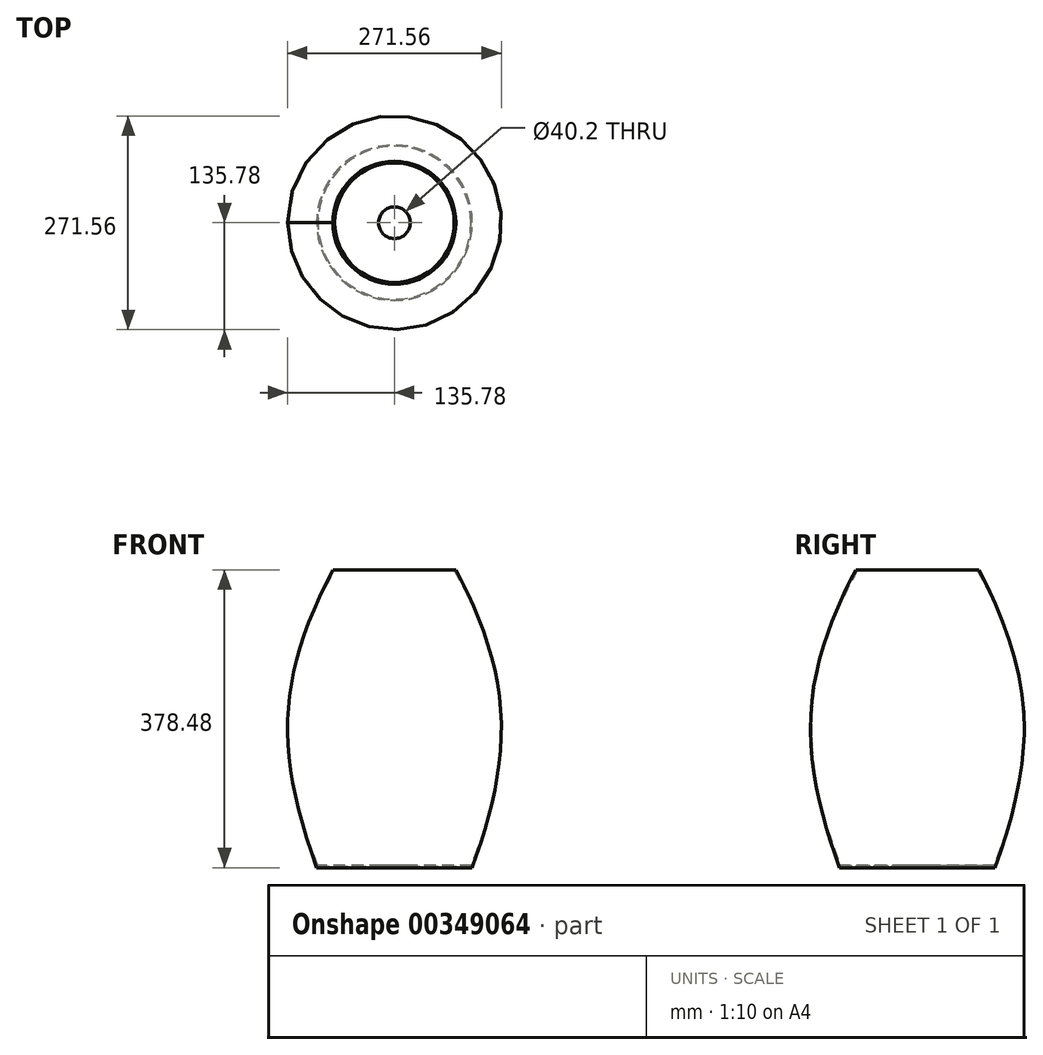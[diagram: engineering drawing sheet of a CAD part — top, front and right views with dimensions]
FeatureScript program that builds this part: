
annotation { "Feature Type Name" : "Feature", "Feature Type Description" : "" }
export const myFeature = defineFeature(function(context is Context, id is Id, definition is map)
    precondition{}
    {
        {
            var Q0;
            Q0=qCreatedBy(makeId("Top.planeOp"),FACE);
            var sketch = newSketch(context, id + "F0", { "sketchPlane" : qUnion([Q0])});
            skCircle(sketch, "E0", {"center": v(0, 0) * mm, "radius": 98.5 * mm});
            skLineSegment(sketch, "E1", {"start": v(0, 0) * mm, "end": v(133.35, 0) * mm, "construction": true});
            skLineSegment(sketch, "E2", {"start": v(133.35, 0) * mm, "end": v(0, 0) * mm, "construction": true});
            skLineSegment(sketch, "E3", {"start": v(0, 0) * mm, "end": v(0, 114.26) * mm, "construction": true});
            skSolve(sketch);
        }
        {
            var Q0;
            Q0 = qSketchRegion(id + "F0", true);
            extrude(context, id + "F1", {"entities" : qUnion([Q0]), "depth" : 3 * mm});
        }
        {
            var Q0;
            Q0=sQuery(id+"F0.wireOp",VERTEX,"E1.start");
            var Q1;
            Q1=makeQuery(id+"F1.opExtrude","SWEPT_BODY",BODY,{"disambiguationData":[OSD([sQuery(id+"F0.wireOp",EDGE,"E0")])]});
            hole(context, id + "F2", {"style" : HoleStyle.SIMPLE, "endStyle" : HoleEndStyle.THROUGH, "oppositeDirection" : true, "holeDiameter" : 40.2 * mm, "isTappedThrough" : true, "tappedDepth" : 12 * mm, "tapClearance" : 3, "locations" : qUnion([Q0]), "scope" : qUnion([Q1])});
        }
        {
            var Q0;
            Q0=qCreatedBy(makeId("Front.planeOp"),FACE);
            var sketch = newSketch(context, id + "F3", { "sketchPlane" : qUnion([Q0])});
            skLineSegment(sketch, "E4", {"start": v(0, 0) * mm, "end": v(0, 95.24) * mm, "construction": true});
            skFitSpline(sketch, "E5", {"points": [v(-98.74, 0) * mm, v(-77.33, 380) * mm], "startDerivative": vector(-164.6, 454.53) * mm, "endDerivative": vector(213.08, 407.5) * mm});
            skFitSpline(sketch, "E6.0", {"points": [v(-96.86, 0.68) * mm, v(-110.56, 38.49) * mm, v(-125.44, 89.64) * mm, v(-133.78, 151.48) * mm, v(-134.23, 195.9) * mm, v(-128.8, 239.57) * mm, v(-113.67, 298.46) * mm, v(-93.27, 345.19) * mm, v(-75.56, 379.07) * mm]});
            skLineSegment(sketch, "E7", {"start": v(-78.12, 378.48) * mm, "end": v(-75.87, 378.48) * mm});
            skLineSegment(sketch, "E8", {"start": v(-97.25, 1.75) * mm, "end": v(-98.74, 0) * mm});
            skSolve(sketch);
        }
        {
            var Q0;
            Q0=makeQuery(id+"F3.imprint","IMPRINT",FACE,{"disambiguationData":[TD([[makeQuery(id+"F3.imprint","IMPRINT",EDGE,{"derivedFrom":sQuery(id+"F3.wireOp",EDGE,"E5")}),-1.0]])]});
            var Q1;
            Q1=sQuery(id+"F3.wireOp",EDGE,"E6.0");
            var Q2;
            Q2=sQuery(id+"F3.wireOp",EDGE,"E4");
            revolve(context, id + "F4", {"entities" : qUnion([Q0]), "surfaceEntities" : qUnion([Q1]), "axis" : qUnion([Q2]), "revolveType" : RevolveType.FULL});
        }
    });
